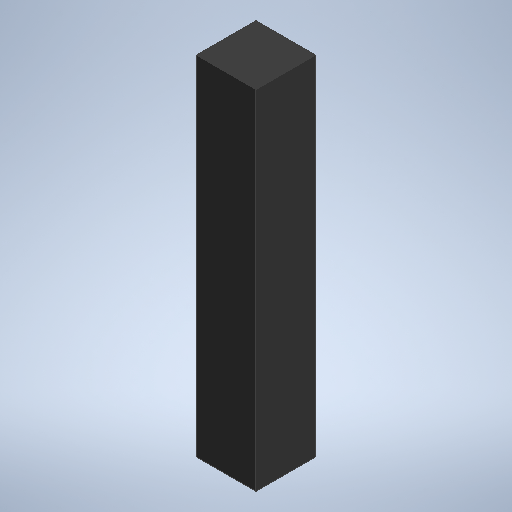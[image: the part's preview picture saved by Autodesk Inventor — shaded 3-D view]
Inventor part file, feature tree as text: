
AUTODESK INVENTOR PART (.ipt)
format: ipt  version: 2025.1 (Build 291241020, 241B)  size: 258,560 bytes
history: native  units: mm
features: extrude x2, sketch x2, projected_geometry x1
ambient origin geometry x8: Origin, YZ Plane, XZ Plane, XY Plane, X Axis, Y Axis, Z Axis, Center Point
bodies: Solid1 (feature_tree)
feature tree (5):
  extrude  "Extrusion1"  Depth=2.4mm
  extrude  "Extrusion2"  Depth=0.79mm
  sketch  "Sketch1"  dims[d0=2.4mm d1=2.4mm]
  sketch  "Sketch2"  dims[d2=0.79mm d3=0.79mm d4=14.0mm d5=0.0mm d6=2.0mm d7=0.0mm]
  projected_geometry  "Projected Loop1"
